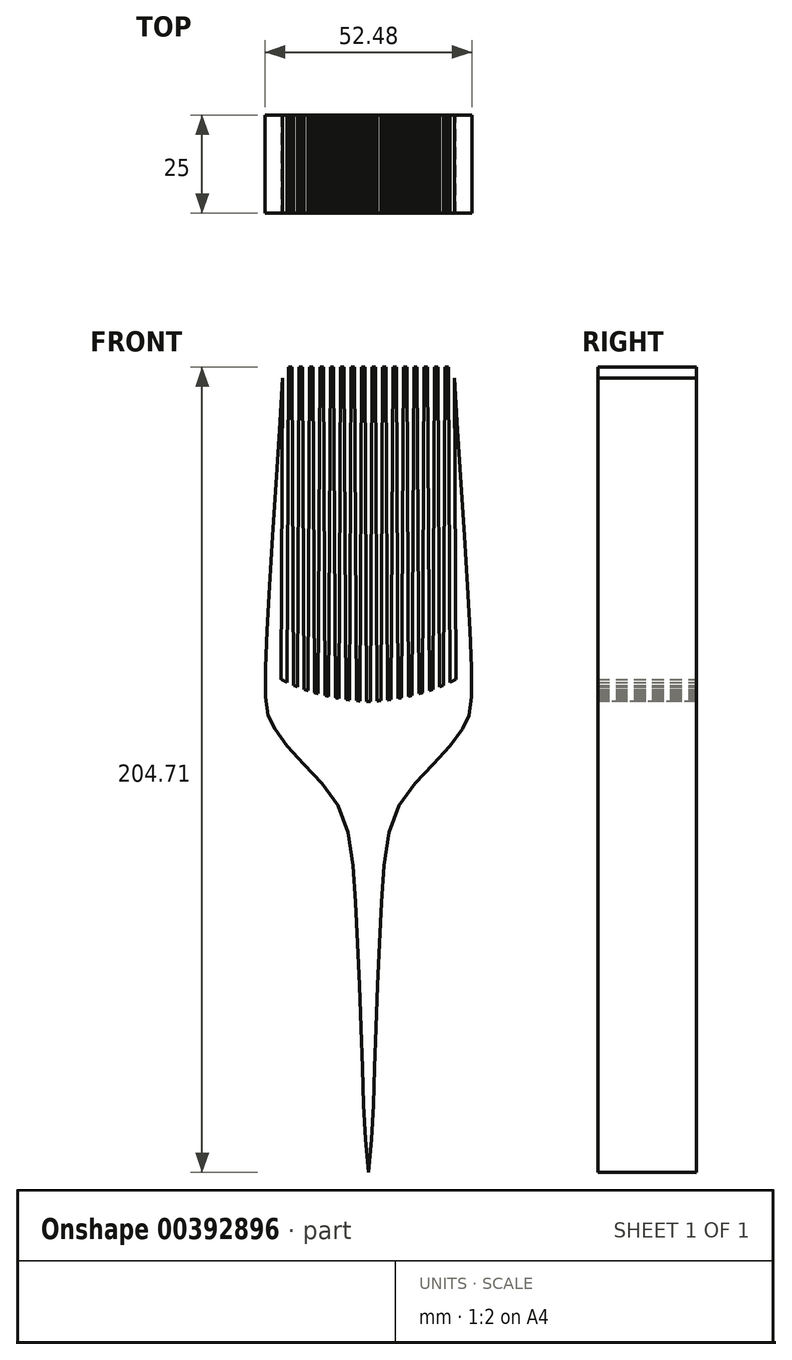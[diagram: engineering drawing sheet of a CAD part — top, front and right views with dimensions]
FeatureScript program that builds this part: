
annotation { "Feature Type Name" : "Feature", "Feature Type Description" : "" }
export const myFeature = defineFeature(function(context is Context, id is Id, definition is map)
    precondition{}
    {
        {
            var Q0;
            Q0=qCreatedBy(makeId("Front.planeOp"),FACE);
            var sketch = newSketch(context, id + "F0", { "sketchPlane" : qUnion([Q0])});
            skLineSegment(sketch, "E0", {"start": v(0, 127.96) * mm, "end": v(0, -147) * mm, "construction": true});
            skFitSpline(sketch, "E1", {"points": [v(-21.87, 94.24) * mm, v(-25.56, 34.85) * mm, v(-25.94, 10.66) * mm, v(-24.18, 5.66) * mm, v(-17.28, -3.06) * mm, v(-7.16, -15.36) * mm, v(-3.22, -40.8) * mm, v(-1.55, -79.78) * mm, v(0, -107.59) * mm], "startDerivative": vector(-15.48, -296.36) * mm, "endDerivative": vector(25.01, -192.64) * mm});
            skFitSpline(sketch, "E2", {"points": [v(-22.22, 17.75) * mm, v(0, 12.14) * mm], "startDerivative": vector(31, -16.48) * mm, "endDerivative": vector(0.41, 0) * mm});
            skFitSpline(sketch, "E3", {"points": [v(-21.87, 94.24) * mm, v(0, 96.44) * mm], "startDerivative": vector(15.35, 5.12) * mm, "endDerivative": vector(6.26, -0.85) * mm});
            skFitSpline(sketch, "E4.MirrorCS", {"points": [v(21.87, 94.24) * mm, v(0, 96.44) * mm], "startDerivative": vector(-15.35, 5.12) * mm, "endDerivative": vector(-6.26, -0.85) * mm});
            skFitSpline(sketch, "E5.MirrorCS", {"points": [v(22.22, 17.75) * mm, v(0, 12.14) * mm], "startDerivative": vector(-31, -16.48) * mm, "endDerivative": vector(-0.41, 0) * mm});
            skFitSpline(sketch, "E6.MirrorCS", {"points": [v(21.87, 94.24) * mm, v(25.56, 34.85) * mm, v(25.94, 10.66) * mm, v(24.18, 5.66) * mm, v(17.28, -3.06) * mm, v(7.16, -15.36) * mm, v(3.22, -40.8) * mm, v(1.55, -79.78) * mm, v(0, -107.59) * mm], "startDerivative": vector(15.48, -296.36) * mm, "endDerivative": vector(-25.01, -192.64) * mm});
            skPoint(sketch, "E7", {"position": v(0, 109.28) * mm});
            skLineSegment(sketch, "E8", {"start": v(-22.22, 17.75) * mm, "end": v(-21.87, 94.24) * mm});
            skLineSegment(sketch, "E9", {"start": v(22.22, 17.75) * mm, "end": v(21.87, 94.24) * mm});
            skSolve(sketch);
        }
        {
            var Q0;
            Q0=qCreatedBy(makeId("Front.planeOp"),FACE);
            var sketch = newSketch(context, id + "F1", { "sketchPlane" : qUnion([Q0])});
            skLineSegment(sketch, "E10", {"start": v(-18.99, 8.58) * mm, "end": v(-19.44, 97.12) * mm});
            skLineSegment(sketch, "E11", {"start": v(-19.87, 18.52) * mm, "end": v(-19.87, 97.12) * mm, "construction": true});
            skLineSegment(sketch, "E12.MirrorCS", {"start": v(-20.76, 8.58) * mm, "end": v(-20.31, 97.12) * mm});
            skLineSegment(sketch, "E13", {"start": v(-20.31, 97.12) * mm, "end": v(-19.44, 97.12) * mm});
            skLineSegment(sketch, "E14", {"start": v(-20.76, 8.58) * mm, "end": v(-18.99, 8.58) * mm});
            skLineSegment(sketch, "E15.1.0.0", {"start": v(-16.34, 8.58) * mm, "end": v(-16.79, 97.12) * mm});
            skLineSegment(sketch, "E15.1.0.1", {"start": v(-18.11, 8.58) * mm, "end": v(-17.66, 97.12) * mm});
            skLineSegment(sketch, "E15.1.0.2", {"start": v(-18.11, 8.58) * mm, "end": v(-16.34, 8.58) * mm});
            skLineSegment(sketch, "E15.1.0.3", {"start": v(-17.66, 97.12) * mm, "end": v(-16.79, 97.12) * mm});
            skLineSegment(sketch, "E15.2.0.0", {"start": v(-13.69, 8.58) * mm, "end": v(-14.14, 97.12) * mm});
            skLineSegment(sketch, "E15.2.0.1", {"start": v(-15.46, 8.58) * mm, "end": v(-15.01, 97.12) * mm});
            skLineSegment(sketch, "E15.2.0.2", {"start": v(-15.46, 8.58) * mm, "end": v(-13.69, 8.58) * mm});
            skLineSegment(sketch, "E15.2.0.3", {"start": v(-15.01, 97.12) * mm, "end": v(-14.14, 97.12) * mm});
            skLineSegment(sketch, "E15.3.0.0", {"start": v(-11.04, 8.58) * mm, "end": v(-11.49, 97.12) * mm});
            skLineSegment(sketch, "E15.3.0.1", {"start": v(-12.81, 8.58) * mm, "end": v(-12.36, 97.12) * mm});
            skLineSegment(sketch, "E15.3.0.2", {"start": v(-12.81, 8.58) * mm, "end": v(-11.04, 8.58) * mm});
            skLineSegment(sketch, "E15.3.0.3", {"start": v(-12.36, 97.12) * mm, "end": v(-11.49, 97.12) * mm});
            skLineSegment(sketch, "E15.4.0.0", {"start": v(-8.39, 8.58) * mm, "end": v(-8.84, 97.12) * mm});
            skLineSegment(sketch, "E15.4.0.1", {"start": v(-10.16, 8.58) * mm, "end": v(-9.71, 97.12) * mm});
            skLineSegment(sketch, "E15.4.0.2", {"start": v(-10.16, 8.58) * mm, "end": v(-8.39, 8.58) * mm});
            skLineSegment(sketch, "E15.4.0.3", {"start": v(-9.71, 97.12) * mm, "end": v(-8.84, 97.12) * mm});
            skLineSegment(sketch, "E15.5.0.0", {"start": v(-5.74, 8.58) * mm, "end": v(-6.19, 97.12) * mm});
            skLineSegment(sketch, "E15.5.0.1", {"start": v(-7.51, 8.58) * mm, "end": v(-7.06, 97.12) * mm});
            skLineSegment(sketch, "E15.5.0.2", {"start": v(-7.51, 8.58) * mm, "end": v(-5.74, 8.58) * mm});
            skLineSegment(sketch, "E15.5.0.3", {"start": v(-7.06, 97.12) * mm, "end": v(-6.19, 97.12) * mm});
            skLineSegment(sketch, "E15.6.0.0", {"start": v(-3.09, 8.58) * mm, "end": v(-3.54, 97.12) * mm});
            skLineSegment(sketch, "E15.6.0.1", {"start": v(-4.86, 8.58) * mm, "end": v(-4.41, 97.12) * mm});
            skLineSegment(sketch, "E15.6.0.2", {"start": v(-4.86, 8.58) * mm, "end": v(-3.09, 8.58) * mm});
            skLineSegment(sketch, "E15.6.0.3", {"start": v(-4.41, 97.12) * mm, "end": v(-3.54, 97.12) * mm});
            skLineSegment(sketch, "E15.7.0.0", {"start": v(-0.44, 8.58) * mm, "end": v(-0.89, 97.12) * mm});
            skLineSegment(sketch, "E15.7.0.1", {"start": v(-2.21, 8.58) * mm, "end": v(-1.76, 97.12) * mm});
            skLineSegment(sketch, "E15.7.0.2", {"start": v(-2.21, 8.58) * mm, "end": v(-0.44, 8.58) * mm});
            skLineSegment(sketch, "E15.7.0.3", {"start": v(-1.76, 97.12) * mm, "end": v(-0.89, 97.12) * mm});
            skLineSegment(sketch, "E15.8.0.0", {"start": v(2.21, 8.58) * mm, "end": v(1.76, 97.12) * mm});
            skLineSegment(sketch, "E15.8.0.1", {"start": v(0.44, 8.58) * mm, "end": v(0.89, 97.12) * mm});
            skLineSegment(sketch, "E15.8.0.2", {"start": v(0.44, 8.58) * mm, "end": v(2.21, 8.58) * mm});
            skLineSegment(sketch, "E15.8.0.3", {"start": v(0.89, 97.12) * mm, "end": v(1.76, 97.12) * mm});
            skLineSegment(sketch, "E15.9.0.0", {"start": v(4.86, 8.58) * mm, "end": v(4.41, 97.12) * mm});
            skLineSegment(sketch, "E15.9.0.1", {"start": v(3.09, 8.58) * mm, "end": v(3.54, 97.12) * mm});
            skLineSegment(sketch, "E15.9.0.2", {"start": v(3.09, 8.58) * mm, "end": v(4.86, 8.58) * mm});
            skLineSegment(sketch, "E15.9.0.3", {"start": v(3.54, 97.12) * mm, "end": v(4.41, 97.12) * mm});
            skLineSegment(sketch, "E15.10.0.0", {"start": v(7.51, 8.58) * mm, "end": v(7.06, 97.12) * mm});
            skLineSegment(sketch, "E15.10.0.1", {"start": v(5.74, 8.58) * mm, "end": v(6.19, 97.12) * mm});
            skLineSegment(sketch, "E15.10.0.2", {"start": v(5.74, 8.58) * mm, "end": v(7.51, 8.58) * mm});
            skLineSegment(sketch, "E15.10.0.3", {"start": v(6.19, 97.12) * mm, "end": v(7.06, 97.12) * mm});
            skLineSegment(sketch, "E15.11.0.0", {"start": v(10.16, 8.58) * mm, "end": v(9.71, 97.12) * mm});
            skLineSegment(sketch, "E15.11.0.1", {"start": v(8.39, 8.58) * mm, "end": v(8.84, 97.12) * mm});
            skLineSegment(sketch, "E15.11.0.2", {"start": v(8.39, 8.58) * mm, "end": v(10.16, 8.58) * mm});
            skLineSegment(sketch, "E15.11.0.3", {"start": v(8.84, 97.12) * mm, "end": v(9.71, 97.12) * mm});
            skLineSegment(sketch, "E15.12.0.0", {"start": v(12.81, 8.58) * mm, "end": v(12.36, 97.12) * mm});
            skLineSegment(sketch, "E15.12.0.1", {"start": v(11.04, 8.58) * mm, "end": v(11.49, 97.12) * mm});
            skLineSegment(sketch, "E15.12.0.2", {"start": v(11.04, 8.58) * mm, "end": v(12.81, 8.58) * mm});
            skLineSegment(sketch, "E15.12.0.3", {"start": v(11.49, 97.12) * mm, "end": v(12.36, 97.12) * mm});
            skLineSegment(sketch, "E15.13.0.0", {"start": v(15.46, 8.58) * mm, "end": v(15.01, 97.12) * mm});
            skLineSegment(sketch, "E15.13.0.1", {"start": v(13.69, 8.58) * mm, "end": v(14.14, 97.12) * mm});
            skLineSegment(sketch, "E15.13.0.2", {"start": v(13.69, 8.58) * mm, "end": v(15.46, 8.58) * mm});
            skLineSegment(sketch, "E15.13.0.3", {"start": v(14.14, 97.12) * mm, "end": v(15.01, 97.12) * mm});
            skLineSegment(sketch, "E15.14.0.0", {"start": v(18.11, 8.58) * mm, "end": v(17.66, 97.12) * mm});
            skLineSegment(sketch, "E15.14.0.1", {"start": v(16.34, 8.58) * mm, "end": v(16.79, 97.12) * mm});
            skLineSegment(sketch, "E15.14.0.2", {"start": v(16.34, 8.58) * mm, "end": v(18.11, 8.58) * mm});
            skLineSegment(sketch, "E15.14.0.3", {"start": v(16.79, 97.12) * mm, "end": v(17.66, 97.12) * mm});
            skLineSegment(sketch, "E15.15.0.0", {"start": v(20.76, 8.58) * mm, "end": v(20.31, 97.12) * mm});
            skLineSegment(sketch, "E15.15.0.1", {"start": v(18.99, 8.58) * mm, "end": v(19.44, 97.12) * mm});
            skLineSegment(sketch, "E15.15.0.2", {"start": v(18.99, 8.58) * mm, "end": v(20.76, 8.58) * mm});
            skLineSegment(sketch, "E15.15.0.3", {"start": v(19.44, 97.12) * mm, "end": v(20.31, 97.12) * mm});
            skLineSegment(sketch, "E15.direction1", {"start": v(-20.76, 8.58) * mm, "end": v(-18.11, 8.58) * mm, "construction": true});
            skPoint(sketch, "E16", {"position": v(-1.33, 97.12) * mm});
            skLineSegment(sketch, "E17", {"start": v(-0.89, 97.12) * mm, "end": v(0.89, 97.12) * mm, "construction": true});
            skPoint(sketch, "E18", {"position": v(0, 97.12) * mm});
            skSolve(sketch);
        }
        {
            var Q0;
            Q0=makeQuery(id+"F0.imprint","IMPRINT",FACE,{"disambiguationData":[TD([[makeQuery(id+"F0.imprint","IMPRINT",EDGE,{"derivedFrom":sQuery(id+"F0.wireOp",EDGE,"E1")}),1.0]])]});
            extrude(context, id + "F2", {"entities" : qUnion([Q0]), "depth" : 25 * mm});
        }
        {
            var Q0;
            Q0=qSketchRegion(id+"F1",true);
            extrude(context, id + "F3", {"entities" : qUnion([Q0]), "operationType" : NewBodyOperationType.ADD, "depth" : 25 * mm});
        }
    });
